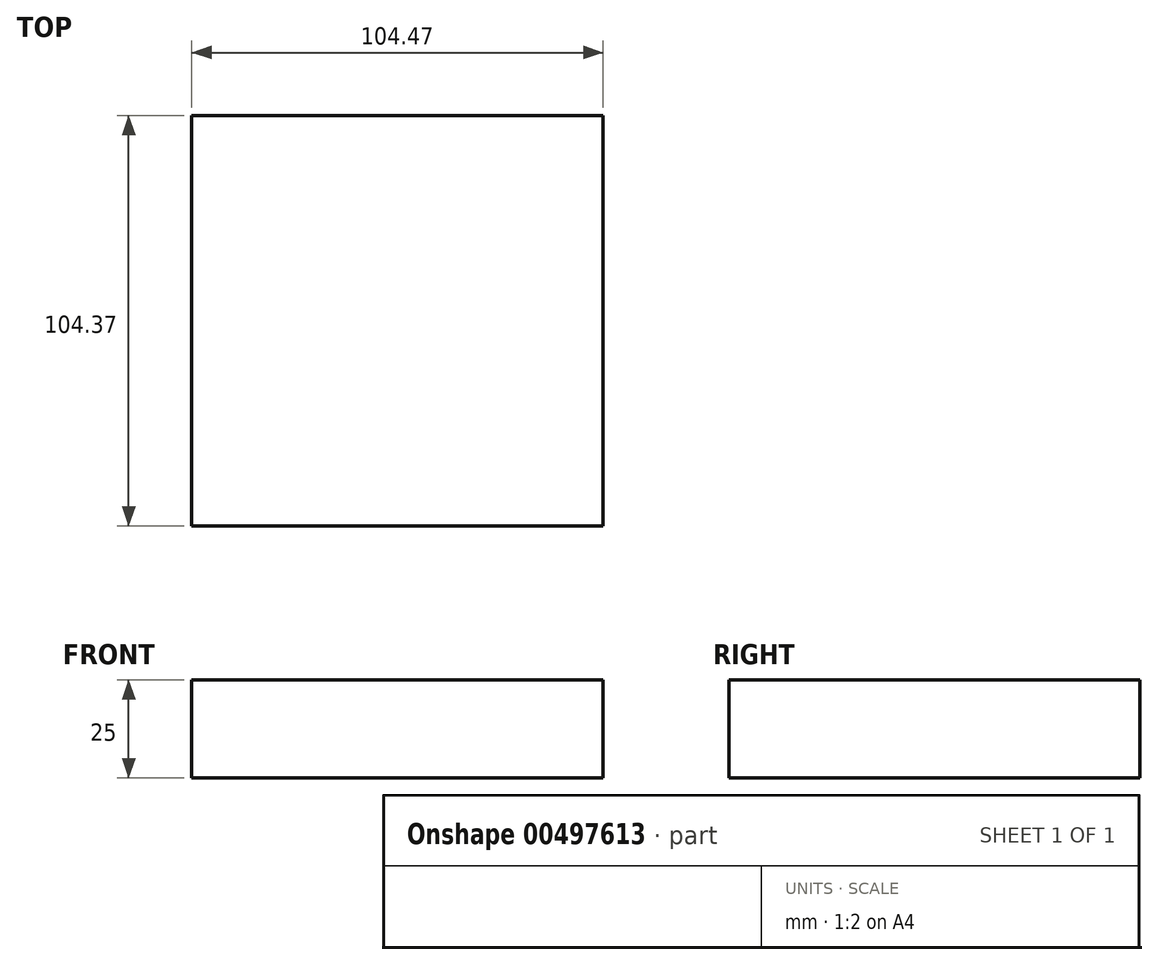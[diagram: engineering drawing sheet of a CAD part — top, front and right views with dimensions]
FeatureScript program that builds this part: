
annotation { "Feature Type Name" : "Feature", "Feature Type Description" : "" }
export const myFeature = defineFeature(function(context is Context, id is Id, definition is map)
    precondition{}
    {
        {
            var Q0;
            Q0=qCreatedBy(makeId("Top.planeOp"),FACE);
            var sketch = newSketch(context, id + "F0", { "sketchPlane" : qUnion([Q0])});
            skLineSegment(sketch, "E0.bottom", {"start": v(0, 0) * mm, "end": v(104.47, 0) * mm});
            skLineSegment(sketch, "E0.top", {"start": v(0, -104.37) * mm, "end": v(104.47, -104.37) * mm});
            skLineSegment(sketch, "E0.left", {"start": v(0, 0) * mm, "end": v(0, -104.37) * mm});
            skLineSegment(sketch, "E0.right", {"start": v(104.47, 0) * mm, "end": v(104.47, -104.37) * mm});
            skPoint(sketch, "E1", {"position": v(47.07, -51.72) * mm});
            skSolve(sketch);
        }
        {
            var Q0;
            Q0 = qSketchRegion(id + "F0", true);
            extrude(context, id + "F1", {"entities" : qUnion([Q0]), "depth" : 25 * mm, "offsetDistance" : 25 * mm});
        }
    });
